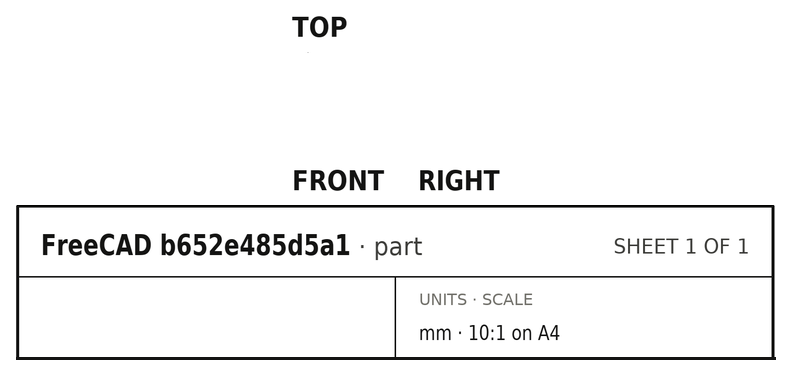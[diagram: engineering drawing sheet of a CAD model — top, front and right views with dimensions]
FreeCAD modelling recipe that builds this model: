
FCSTD DOCUMENT  (FreeCAD 0.21R33694 (Git))
Label: bridge
License: All rights reserved
LicenseURL: http://en.wikipedia.org/wiki/All_rights_reserved
objects: Part::Part2DObjectPython×10, Part::Extrusion×6, App::FeaturePython×4, Part::Cut×3, Part::Feature×2, Part::FeaturePython×2
note: 23 computed .brp shape members not serialized (recipe doc carries the construction recipe); baked Part::Feature solids carry a one-line shape summary decoded from their .brp

FEATURE [Part::Part2DObjectPython] Rectangle  # Draft 2D object (typed FeaturePython)
  Area = 0.2317
  ChamferSize = 0
  Columns = 1
  FilletRadius = 0
  Height = 2.317
  Length = 0.1
  MakeFace = true
  Placement = pos=(-1.31536,-0.172151,0) rot=(0,0,1;0rad)
  Rows = 1
FEATURE [Part::Part2DObjectPython] Rectangle001  # Draft 2D object (typed FeaturePython)
  Area = 0.5
  ChamferSize = 0
  Columns = 1
  FilletRadius = 0
  Height = 1
  Length = 0.5
  MakeFace = true
  Placement = pos=(-1.51536,1.14485,0) rot=(0,0,1;0rad)
  Rows = 1
FEATURE [Part::Part2DObjectPython] Rectangle002  # Draft 2D object (typed FeaturePython)
  Area = 0.5
  ChamferSize = 0
  Columns = 1
  FilletRadius = 0
  Height = 1
  Length = 0.5
  MakeFace = true
  Placement = pos=(-1.51536,-0.172151,0) rot=(0,0,1;0rad)
  Rows = 1
FEATURE [Part::Extrusion] Extrude001
  Base = -> Rectangle001
  Dir = (0,0,1)
  DirMode = 2
  FaceMakerClass = Part::FaceMakerBullseye
  LengthFwd = 0.1
  LengthRev = 0
  Solid = false
  Symmetric = false
FEATURE [Part::Extrusion] Extrude002
  Base = -> Rectangle002
  Dir = (0,0,1)
  DirMode = 2
  FaceMakerClass = Part::FaceMakerBullseye
  LengthFwd = 0.1
  LengthRev = 0
  Solid = false
  Symmetric = false
FEATURE [Part::Extrusion] Extrude003
  Base = -> Rectangle
  Dir = (0,0,1)
  DirMode = 2
  FaceMakerClass = Part::FaceMakerBullseye
  LengthFwd = 0.02
  LengthRev = 0
  Placement = pos=(0,0,0.1) rot=(0,0,1;0rad)
  Solid = false
  Symmetric = false
FEATURE [Part::Part2DObjectPython] Rectangle004  # Draft 2D object (typed FeaturePython)
  Area = 0.5
  ChamferSize = 0
  Columns = 1
  FilletRadius = 0
  Height = 1
  Length = 0.5
  MakeFace = true
  Placement = pos=(-1.51536,-0.172151,0.1) rot=(0,0,1;0rad)
  Rows = 1
FEATURE [Part::Part2DObjectPython] Rectangle005  # Draft 2D object (typed FeaturePython)
  Area = 0.1585
  ChamferSize = 0
  Columns = 1
  FilletRadius = 0
  Height = 0.317
  Length = 0.5
  MakeFace = true
  Placement = pos=(-1.51536,0.827849,0) rot=(0,0,1;0rad)
  Rows = 1
FEATURE [Part::Part2DObjectPython] Rectangle006  # Draft 2D object (typed FeaturePython)
  Area = 0.5
  ChamferSize = 0
  Columns = 1
  FilletRadius = 0
  Height = 1
  Length = 0.5
  MakeFace = true
  Placement = pos=(-1.51536,1.14485,0.1) rot=(0,0,1;0rad)
  Rows = 1
FEATURE [Part::Extrusion] Extrude
  Base = -> Rectangle004
  Dir = (0,0,1)
  DirMode = 2
  FaceMakerClass = Part::FaceMakerBullseye
  LengthFwd = 0.22
  LengthRev = 0
  Solid = false
  Symmetric = false
FEATURE [Part::Extrusion] Extrude004
  Base = -> Rectangle006
  Dir = (0,0,1)
  DirMode = 2
  FaceMakerClass = Part::FaceMakerBullseye
  LengthFwd = 0.22
  LengthRev = 0
  Solid = false
  Symmetric = false
FEATURE [Part::Extrusion] Extrude005
  Base = -> Rectangle005
  Dir = (0,0,1)
  DirMode = 2
  FaceMakerClass = Part::FaceMakerBullseye
  LengthFwd = 0.32
  LengthRev = 0
  Solid = false
  Symmetric = false
FEATURE [Part::Feature] Extrude003001
  Placement = pos=(0,0,0.1) rot=(0,0,1;0rad)
  shape: bbox 0.1 x 2.317 x 0.02 mm, 6 faces (baked)
FEATURE [Part::Feature] Extrude003002
  Placement = pos=(0,0,0.1) rot=(0,0,1;0rad)
  shape: bbox 0.1 x 2.317 x 0.02 mm, 6 faces (baked)
FEATURE [Part::Cut] Cut
  Base = -> Extrude
  Tool = -> Extrude003
FEATURE [Part::Cut] Cut001
  Base = -> Extrude004
  Tool = -> Extrude003001
FEATURE [Part::Cut] Cut002
  Base = -> Extrude005
  Tool = -> Extrude003002
FEATURE [Part::FeaturePython] BooleanFragments  # WARN: FeaturePython — macro-defined, semantics opaque (R4)
  Mode = 0
  Objects = -> [Extrude001,Extrude002,Cut,Cut001,Cut002]
  Tolerance = 0
FEATURE [Part::FeaturePython] Clone  label="scaled"  # Draft clone (typed FeaturePython)
  AttacherType = Attacher::AttachEngine3D
  Fuse = false
  Objects = -> [BooleanFragments]
  Scale = (0.001,0.001,0.001)
FEATURE [Part::Part2DObjectPython] Rectangle007  label="_P1"  # Draft 2D object (typed FeaturePython)
  Area = 1.6e-07
  ChamferSize = 0
  Columns = 1
  FilletRadius = 0
  Height = 0.00032
  Length = 0.0005
  MakeFace = true
  Placement = pos=(-0.00151536,-0.000172151,0) rot=(1,0,0;1.5708rad)
  Rows = 1
FEATURE [Part::Part2DObjectPython] Line  label="_PV1"  # Draft 2D object (typed FeaturePython)
  Area = 0
  ChamferSize = 0
  Closed = false
  End = (-0.00126536,-0.000172151,0.0001)
  FilletRadius = 0
  Length = 0.0001
  MakeFace = true
  Placement = pos=(-0.00126536,-0.000172151,0) rot=(1,0,0;1.5708rad)
  Points = (2) [(0,0,0),(0,0.0001,2.71051e-20)]
  Start = (-0.00126536,-0.000172151,0)
  Subdivisions = 0
FEATURE [Part::Part2DObjectPython] Rectangle008  label="_P2"  # Draft 2D object (typed FeaturePython)
  Area = 1.6e-07
  ChamferSize = 0
  Columns = 1
  FilletRadius = 0
  Height = 0.00032
  Length = 0.0005
  MakeFace = true
  Placement = pos=(-0.00151536,0.00214485,0.00032) rot=(-1,0,0;1.5708rad)
  Rows = 1
FEATURE [Part::Part2DObjectPython] Line001  label="_PV2"  # Draft 2D object (typed FeaturePython)
  Area = 0
  ChamferSize = 0
  Closed = false
  End = (-0.00126536,0.00214485,0.0001)
  FilletRadius = 0
  Length = 0.0001
  MakeFace = true
  Placement = pos=(-0.00126536,0.00214485,0) rot=(-1,0,0;1.5708rad)
  Points = (2) [(0,0,0),(0,-0.0001,0)]
  Start = (-0.00126536,0.00214485,0)
  Subdivisions = 0
FEATURE [App::FeaturePython] Text  label="_L1(1,voltage){V1}"  # WARN: FeaturePython — macro-defined, semantics opaque (R4)
  Placement = pos=(-0.00142938,0.00214485,-0.000182546) rot=(-1,0,0;1.5708rad)
  Text = .
FEATURE [App::FeaturePython] Text001  label="_S2(PV){2}"  # WARN: FeaturePython — macro-defined, semantics opaque (R4)
  Placement = pos=(-0.00142938,0.00214485,-0.000182546) rot=(-1,0,0;1.5708rad)
  Text = .
FEATURE [App::FeaturePython] Text002  label="_S1(PV){1}"  # WARN: FeaturePython — macro-defined, semantics opaque (R4)
  Placement = pos=(-0.00142938,0.00214485,-0.000182546) rot=(-1,0,0;1.5708rad)
  Text = .
FEATURE [App::FeaturePython] Text003  label="_L2(2,voltage){V2}"  # WARN: FeaturePython — macro-defined, semantics opaque (R4)
  Placement = pos=(-0.00142938,0.00214485,-0.000182546) rot=(-1,0,0;1.5708rad)
  Text = .
